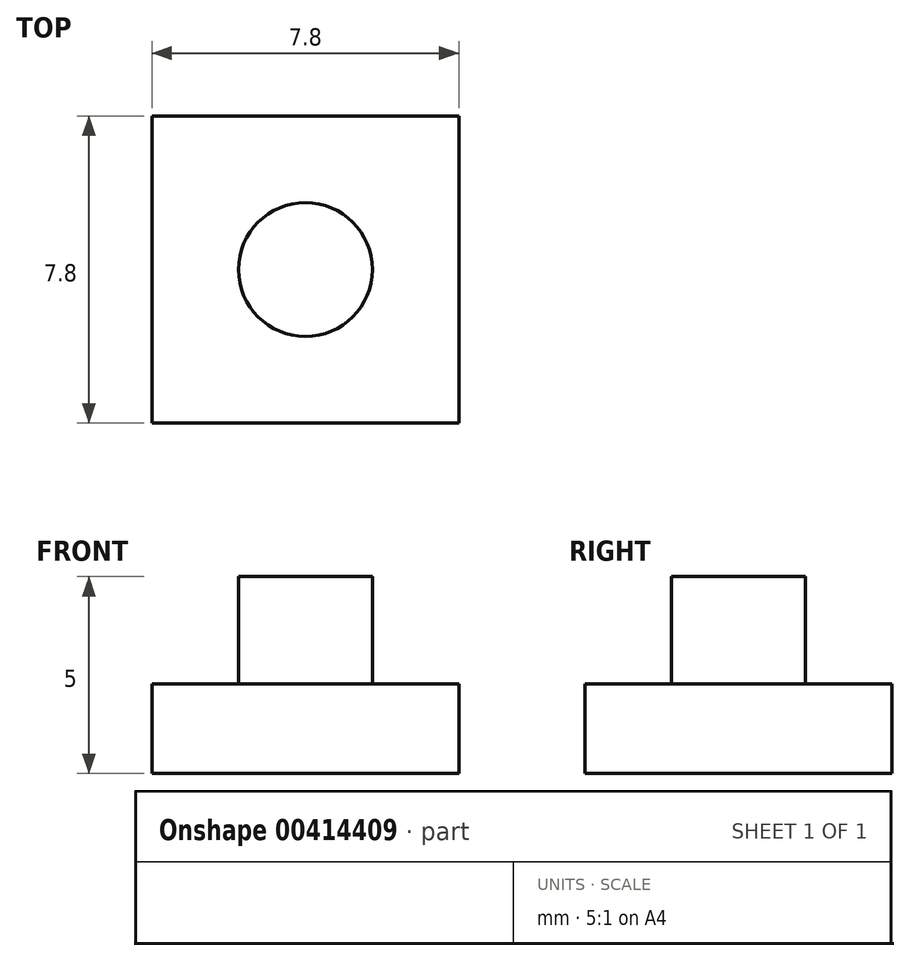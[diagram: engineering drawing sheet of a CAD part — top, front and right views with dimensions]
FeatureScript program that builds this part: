
annotation { "Feature Type Name" : "Feature", "Feature Type Description" : "" }
export const myFeature = defineFeature(function(context is Context, id is Id, definition is map)
    precondition{}
    {
        {
            var Q0;
            Q0=qCreatedBy(makeId("Top.planeOp"),FACE);
            var sketch = newSketch(context, id + "F0", { "sketchPlane" : qUnion([Q0])});
            skCircle(sketch, "E0", {"center": v(0, 0) * mm, "radius": 1.7 * mm});
            skLineSegment(sketch, "E1.bottom", {"start": v(-3.9, 3.9) * mm, "end": v(3.9, 3.9) * mm});
            skLineSegment(sketch, "E1.top", {"start": v(-3.9, -3.9) * mm, "end": v(3.9, -3.9) * mm});
            skLineSegment(sketch, "E1.left", {"start": v(-3.9, 3.9) * mm, "end": v(-3.9, -3.9) * mm});
            skLineSegment(sketch, "E1.right", {"start": v(3.9, 3.9) * mm, "end": v(3.9, -3.9) * mm});
            skSolve(sketch);
        }
        {
            var Q0;
            Q0=makeQuery(id+"F0.imprint","IMPRINT",FACE,{"disambiguationData":[TD([[makeQuery(id+"F0.imprint","IMPRINT",EDGE,{"derivedFrom":sQuery(id+"F0.wireOp",EDGE,"E0")}),-1.0]])]});
            var Q1;
            Q1=makeQuery(id+"F0.imprint","IMPRINT",FACE,{"disambiguationData":[TD([[makeQuery(id+"F0.imprint","IMPRINT",EDGE,{"derivedFrom":sQuery(id+"F0.wireOp",EDGE,"E0")}),1.0]])]});
            extrude(context, id + "F1", {"entities" : qUnion([Q0, Q1]), "depth" : 2.27 * mm});
        }
        {
            var Q0;
            Q0=makeQuery(id+"F0.imprint","IMPRINT",FACE,{"disambiguationData":[TD([[makeQuery(id+"F0.imprint","IMPRINT",EDGE,{"derivedFrom":sQuery(id+"F0.wireOp",EDGE,"E0")}),1.0]])]});
            extrude(context, id + "F2", {"entities" : qUnion([Q0]), "operationType" : NewBodyOperationType.ADD, "depth" : 5 * mm});
        }
    });
